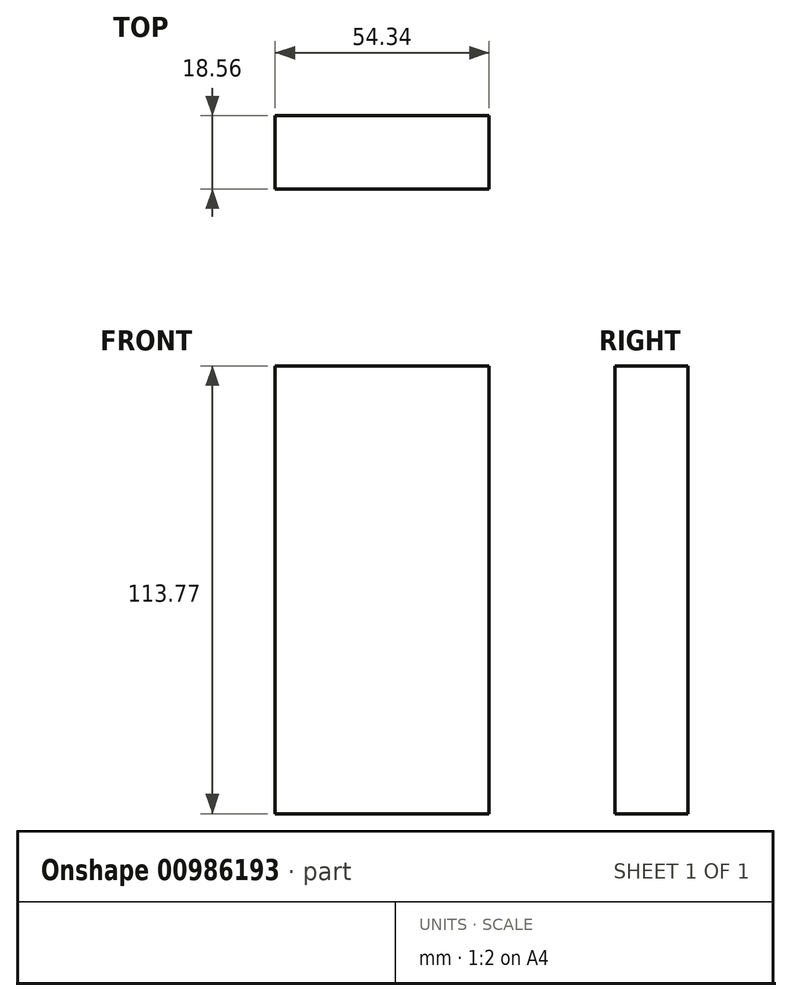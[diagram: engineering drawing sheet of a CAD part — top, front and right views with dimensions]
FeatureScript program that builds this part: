
annotation { "Feature Type Name" : "Feature", "Feature Type Description" : "" }
export const myFeature = defineFeature(function(context is Context, id is Id, definition is map)
    precondition{}
    {
        {
            var Q0;
            Q0=qCreatedBy(makeId("Front.planeOp"),FACE);
            var sketch = newSketch(context, id + "F0", { "sketchPlane" : qUnion([Q0])});
            skLineSegment(sketch, "E0.bottom", {"start": v(27.36, 64.78) * mm, "end": v(-26.98, 64.78) * mm});
            skLineSegment(sketch, "E0.top", {"start": v(27.36, -48.99) * mm, "end": v(-26.98, -48.99) * mm});
            skLineSegment(sketch, "E0.left", {"start": v(27.36, 64.78) * mm, "end": v(27.36, -48.99) * mm});
            skLineSegment(sketch, "E0.right", {"start": v(-26.98, 64.78) * mm, "end": v(-26.98, -48.99) * mm});
            skSolve(sketch);
        }
        {
            var Q0;
            Q0 = qSketchRegion(id + "F0", true);
            extrude(context, id + "F1", {"entities" : qUnion([Q0]), "depth" : 18.56 * mm, "offsetDistance" : 25.4 * mm});
        }
    });
